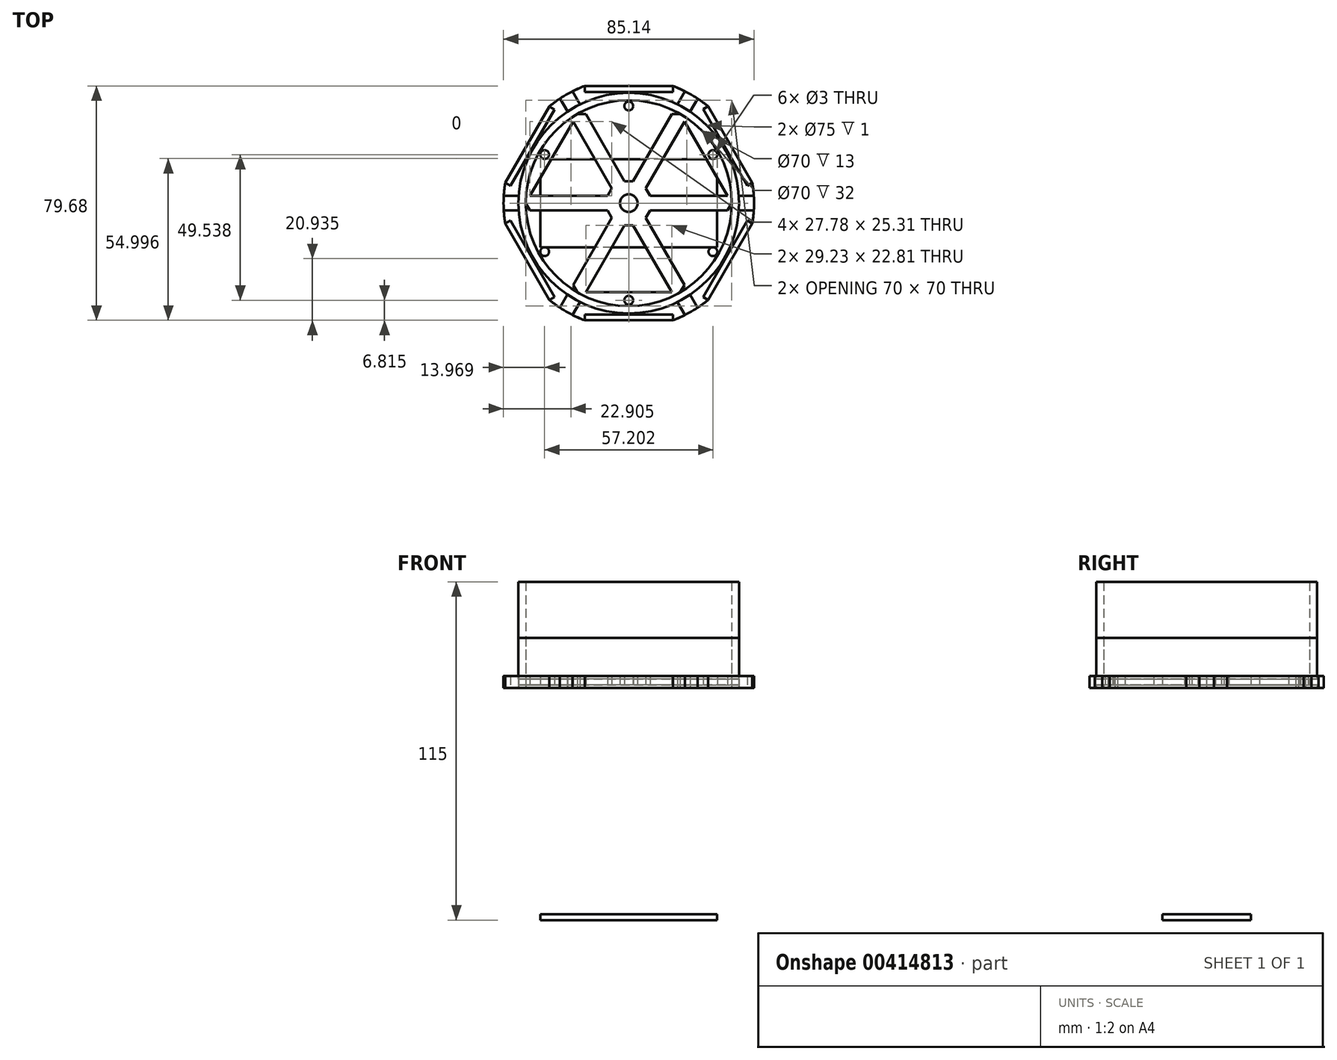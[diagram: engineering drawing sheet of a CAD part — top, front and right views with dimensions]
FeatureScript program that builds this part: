
annotation { "Feature Type Name" : "Feature", "Feature Type Description" : "" }
export const myFeature = defineFeature(function(context is Context, id is Id, definition is map)
    precondition{}
    {
        {
            var Q0;
            Q0=qCreatedBy(makeId("Front.planeOp"),FACE);
            var sketch = newSketch(context, id + "F0", { "sketchPlane" : qUnion([Q0])});
            skPoint(sketch, "E0.0.midPoint", {"position": v(34.2, -19.75) * mm});
            skLineSegment(sketch, "E1", {"start": v(-48.36, -0.03) * mm, "end": v(42.86, 0) * mm, "construction": true});
            skLineSegment(sketch, "E2", {"start": v(21.2, 36.7) * mm, "end": v(-22.8, -39.5) * mm, "construction": true});
            skLineSegment(sketch, "E3", {"start": v(-21.15, 36.67) * mm, "end": v(22.83, -39.49) * mm, "construction": true});
            skLineSegment(sketch, "E4.bottom", {"start": v(15.02, 37.52) * mm, "end": v(-14.98, 37.51) * mm});
            skLineSegment(sketch, "E4.left", {"start": v(15.02, 37.52) * mm, "end": v(15.07, 39.6) * mm});
            skLineSegment(sketch, "E4.right", {"start": v(-14.98, 37.51) * mm, "end": v(-14.93, 39.62) * mm});
            skPoint(sketch, "E4.middle", {"position": v(-0.03, 39.48) * mm});
            skCircle(sketch, "E5", {"center": v(0, 0) * mm, "radius": 37.5 * mm});
            skLineSegment(sketch, "E6", {"start": v(19, 37.88) * mm, "end": v(16.67, 33.87) * mm});
            skLineSegment(sketch, "E7", {"start": v(16.67, 33.87) * mm, "end": v(18.84, 32.62) * mm});
            skLineSegment(sketch, "E8.MirrorCS", {"start": v(21, 31.37) * mm, "end": v(18.84, 32.62) * mm});
            skLineSegment(sketch, "E9.MirrorCS", {"start": v(23.32, 35.38) * mm, "end": v(21, 31.37) * mm});
            skLineSegment(sketch, "E10.MirrorCS", {"start": v(25, 31.76) * mm, "end": v(26.77, 32.85) * mm});
            skLineSegment(sketch, "E11.MirrorCS", {"start": v(25, 31.76) * mm, "end": v(40, 5.78) * mm});
            skLineSegment(sketch, "E12.MirrorCS", {"start": v(40, 5.78) * mm, "end": v(41.68, 6.81) * mm});
            skLineSegment(sketch, "E13.MirrorCS", {"start": v(-18.97, 37.85) * mm, "end": v(-16.67, 33.87) * mm});
            skLineSegment(sketch, "E14.MirrorCS", {"start": v(-23.3, 35.35) * mm, "end": v(-21, 31.37) * mm});
            skLineSegment(sketch, "E15.MirrorCS", {"start": v(-21, 31.37) * mm, "end": v(-18.84, 32.62) * mm});
            skLineSegment(sketch, "E16.MirrorCS", {"start": v(-16.67, 33.87) * mm, "end": v(-18.84, 32.62) * mm});
            skArc(sketch, "E17", {"start": v(-14.93, 39.62) * mm, "mid": v(-16.97, 38.78) * mm, "end": v(-18.97, 37.85) * mm});
            skArc(sketch, "E18", {"start": v(15.07, 39.6) * mm, "mid": v(17.05, 38.8) * mm, "end": v(19, 37.88) * mm});
            skLineSegment(sketch, "E19.MirrorCS", {"start": v(-39.96, 5.77) * mm, "end": v(-24.96, 31.75) * mm});
            skLineSegment(sketch, "E20.MirrorCS", {"start": v(-24.96, 31.75) * mm, "end": v(-26.81, 32.75) * mm});
            skLineSegment(sketch, "E21.MirrorCS", {"start": v(-39.96, 5.77) * mm, "end": v(-41.8, 6.77) * mm});
            skArc(sketch, "E22.trimOffspring", {"start": v(-23.3, 35.35) * mm, "mid": v(-25.04, 34.13) * mm, "end": v(-26.72, 32.84) * mm});
            skArc(sketch, "E23.trimOffspring", {"start": v(23.32, 35.38) * mm, "mid": v(25.08, 34.16) * mm, "end": v(26.77, 32.85) * mm});
            skLineSegment(sketch, "E24", {"start": v(0, 0) * mm, "end": v(32.5, 18.77) * mm, "construction": true});
            skLineSegment(sketch, "E25", {"start": v(0, 0) * mm, "end": v(-32.46, 18.76) * mm, "construction": true});
            skArc(sketch, "E26.MirrorCS", {"start": v(42.3, 2.52) * mm, "mid": v(42.12, 4.65) * mm, "end": v(41.83, 6.77) * mm});
            skLineSegment(sketch, "E27.MirrorCS", {"start": v(42.3, 2.52) * mm, "end": v(37.67, 2.52) * mm});
            skLineSegment(sketch, "E28.MirrorCS", {"start": v(37.67, 2.52) * mm, "end": v(37.67, 0.02) * mm});
            skArc(sketch, "E29.MirrorCS", {"start": v(-42.26, 2.55) * mm, "mid": v(-42.08, 4.66) * mm, "end": v(-41.8, 6.76) * mm});
            skLineSegment(sketch, "E30.MirrorCS", {"start": v(-42.26, 2.55) * mm, "end": v(-37.67, 2.54) * mm});
            skLineSegment(sketch, "E31.MirrorCS", {"start": v(-37.67, 2.54) * mm, "end": v(-37.67, 0.04) * mm});
            skLineSegment(sketch, "E32.MirrorCS", {"start": v(25.02, -31.76) * mm, "end": v(26.8, -32.85) * mm});
            skLineSegment(sketch, "E33.MirrorCS", {"start": v(-39.95, -5.83) * mm, "end": v(-41.8, -6.82) * mm});
            skLineSegment(sketch, "E34.MirrorCS", {"start": v(40, -5.77) * mm, "end": v(41.68, -6.8) * mm});
            skLineSegment(sketch, "E35.MirrorCS", {"start": v(-24.93, -31.8) * mm, "end": v(-26.78, -32.8) * mm});
            skArc(sketch, "E36.MirrorCS", {"start": v(23.35, -35.39) * mm, "mid": v(25.1, -34.16) * mm, "end": v(26.8, -32.85) * mm});
            skLineSegment(sketch, "E37.MirrorCS", {"start": v(16.7, -33.88) * mm, "end": v(18.87, -32.63) * mm});
            skLineSegment(sketch, "E38.MirrorCS", {"start": v(21.03, -31.37) * mm, "end": v(18.87, -32.63) * mm});
            skLineSegment(sketch, "E39.MirrorCS", {"start": v(-20.98, -31.41) * mm, "end": v(-18.81, -32.66) * mm});
            skLineSegment(sketch, "E40.MirrorCS", {"start": v(-16.65, -33.9) * mm, "end": v(-18.81, -32.66) * mm});
            skArc(sketch, "E41.MirrorCS", {"start": v(-23.27, -35.39) * mm, "mid": v(-25.01, -34.18) * mm, "end": v(-26.7, -32.88) * mm});
            skLineSegment(sketch, "E42.MirrorCS", {"start": v(-23.27, -35.39) * mm, "end": v(-20.98, -31.41) * mm});
            skLineSegment(sketch, "E43.MirrorCS", {"start": v(25.02, -31.76) * mm, "end": v(40, -5.77) * mm});
            skLineSegment(sketch, "E44.MirrorCS", {"start": v(-39.95, -5.83) * mm, "end": v(-24.93, -31.8) * mm});
            skPoint(sketch, "E45.MirrorP", {"position": v(0, -39.5) * mm});
            skLineSegment(sketch, "E46.MirrorCS", {"start": v(42.3, -2.5) * mm, "end": v(37.67, -2.51) * mm});
            skArc(sketch, "E47.MirrorCS", {"start": v(-42.26, -2.6) * mm, "mid": v(-42.07, -4.72) * mm, "end": v(-41.79, -6.82) * mm});
            skArc(sketch, "E48.MirrorCS", {"start": v(42.3, -2.5) * mm, "mid": v(42.13, -4.64) * mm, "end": v(41.84, -6.76) * mm});
            skLineSegment(sketch, "E49.MirrorCS", {"start": v(23.35, -35.39) * mm, "end": v(21.03, -31.37) * mm});
            skLineSegment(sketch, "E50.MirrorCS", {"start": v(15.05, -37.53) * mm, "end": v(-14.95, -37.55) * mm});
            skLineSegment(sketch, "E51.MirrorCS", {"start": v(15.05, -37.53) * mm, "end": v(15.1, -39.62) * mm});
            skArc(sketch, "E52.MirrorCS", {"start": v(15.1, -39.62) * mm, "mid": v(17.09, -38.8) * mm, "end": v(19.02, -37.9) * mm});
            skLineSegment(sketch, "E53.MirrorCS", {"start": v(19.02, -37.9) * mm, "end": v(16.7, -33.88) * mm});
            skLineSegment(sketch, "E54.MirrorCS", {"start": v(-14.95, -37.55) * mm, "end": v(-14.9, -39.65) * mm});
            skArc(sketch, "E55.MirrorCS", {"start": v(-14.9, -39.65) * mm, "mid": v(-16.94, -38.82) * mm, "end": v(-18.94, -37.89) * mm});
            skLineSegment(sketch, "E56.MirrorCS", {"start": v(-18.94, -37.89) * mm, "end": v(-16.65, -33.9) * mm});
            skCircle(sketch, "E57.cCircle", {"center": v(0, 0) * mm, "radius": 35.5 * mm});
            skLineSegment(sketch, "E57.0", {"start": v(35.5, 0) * mm, "end": v(17.75, -30.74) * mm});
            skLineSegment(sketch, "E57.1", {"start": v(17.75, -30.74) * mm, "end": v(-17.75, -30.75) * mm});
            skLineSegment(sketch, "E57.2", {"start": v(-17.75, -30.75) * mm, "end": v(-35.5, 0) * mm});
            skLineSegment(sketch, "E57.3", {"start": v(-35.5, 0) * mm, "end": v(-17.75, 30.74) * mm});
            skLineSegment(sketch, "E57.4", {"start": v(-17.75, 30.74) * mm, "end": v(17.75, 30.75) * mm});
            skLineSegment(sketch, "E57.5", {"start": v(17.75, 30.75) * mm, "end": v(35.5, 0) * mm});
            skLineSegment(sketch, "E58.0", {"start": v(7.6, 0) * mm, "end": v(3.75, -6.55) * mm});
            skLineSegment(sketch, "E58.1", {"start": v(3.75, -6.55) * mm, "end": v(-3.81, -6.54) * mm});
            skLineSegment(sketch, "E58.2", {"start": v(-3.81, -6.54) * mm, "end": v(-7.65, 0) * mm});
            skLineSegment(sketch, "E58.3", {"start": v(-7.65, 0) * mm, "end": v(-3.79, 6.55) * mm});
            skLineSegment(sketch, "E58.4", {"start": v(-3.79, 6.55) * mm, "end": v(3.76, 6.54) * mm});
            skLineSegment(sketch, "E58.5", {"start": v(3.76, 6.54) * mm, "end": v(7.6, 0) * mm});
            skLineSegment(sketch, "E59", {"start": v(21, 31.37) * mm, "end": v(5.23, 4.04) * mm, "construction": true});
            skLineSegment(sketch, "E60", {"start": v(19.2, 28.24) * mm, "end": v(5.23, 4.04) * mm});
            skLineSegment(sketch, "E61.MirrorCS", {"start": v(16.67, 33.87) * mm, "end": v(0.9, 6.54) * mm, "construction": true});
            skLineSegment(sketch, "E62", {"start": v(14.87, 30.75) * mm, "end": v(0.9, 6.54) * mm});
            skLineSegment(sketch, "E63.MirrorCS", {"start": v(-16.67, 33.87) * mm, "end": v(-0.9, 6.54) * mm, "construction": true});
            skLineSegment(sketch, "E64.MirrorCS", {"start": v(-21, 31.37) * mm, "end": v(-5.23, 4.04) * mm, "construction": true});
            skLineSegment(sketch, "E65", {"start": v(-14.87, 30.74) * mm, "end": v(-0.9, 6.54) * mm});
            skLineSegment(sketch, "E66", {"start": v(-19.2, 28.24) * mm, "end": v(-5.23, 4.04) * mm});
            skLineSegment(sketch, "E67.MirrorCS", {"start": v(37.67, 2.52) * mm, "end": v(6.11, 2.51) * mm, "construction": true});
            skLineSegment(sketch, "E68.MirrorCS", {"start": v(37.67, -2.48) * mm, "end": v(6.11, -2.49) * mm, "construction": true});
            skLineSegment(sketch, "E69.MirrorCS", {"start": v(21, -31.37) * mm, "end": v(5.22, -4.05) * mm, "construction": true});
            skLineSegment(sketch, "E70.MirrorCS", {"start": v(16.68, -33.87) * mm, "end": v(0.89, -6.55) * mm, "construction": true});
            skLineSegment(sketch, "E71", {"start": v(34.05, 2.52) * mm, "end": v(6.11, 2.51) * mm});
            skLineSegment(sketch, "E72", {"start": v(34.07, -2.48) * mm, "end": v(6.11, -2.49) * mm});
            skLineSegment(sketch, "E73", {"start": v(5.22, -4.05) * mm, "end": v(19.2, -28.24) * mm});
            skLineSegment(sketch, "E74", {"start": v(0.89, -6.55) * mm, "end": v(14.87, -30.74) * mm});
            skLineSegment(sketch, "E75.MirrorCS", {"start": v(-16.68, -33.87) * mm, "end": v(-0.89, -6.55) * mm, "construction": true});
            skLineSegment(sketch, "E76.MirrorCS", {"start": v(-21, -31.37) * mm, "end": v(-5.25, -4.1) * mm, "construction": true});
            skLineSegment(sketch, "E77.MirrorCS", {"start": v(-37.67, -2.48) * mm, "end": v(-6.11, -2.49) * mm, "construction": true});
            skLineSegment(sketch, "E78.MirrorCS", {"start": v(-37.67, 2.52) * mm, "end": v(-6.11, 2.51) * mm, "construction": true});
            skLineSegment(sketch, "E79", {"start": v(-14.87, -30.75) * mm, "end": v(-0.89, -6.55) * mm});
            skLineSegment(sketch, "E80", {"start": v(-19.2, -28.24) * mm, "end": v(-5.25, -4.1) * mm});
            skLineSegment(sketch, "E81", {"start": v(-6.11, -2.49) * mm, "end": v(-34.07, -2.48) * mm});
            skLineSegment(sketch, "E82", {"start": v(-34.04, 2.52) * mm, "end": v(-6.11, 2.51) * mm});
            skCircle(sketch, "E83", {"center": v(0, 33.97) * mm, "radius": 1.5 * mm});
            skCircle(sketch, "E84.MirrorC", {"center": v(29.43, 16.98) * mm, "radius": 1.5 * mm});
            skCircle(sketch, "E85.MirrorC", {"center": v(-29.38, 17) * mm, "radius": 1.5 * mm});
            skCircle(sketch, "E86.MirrorC", {"center": v(0.03, -34) * mm, "radius": 1.5 * mm});
            skCircle(sketch, "E87.MirrorC", {"center": v(29.44, -16.98) * mm, "radius": 1.5 * mm});
            skCircle(sketch, "E88.MirrorC", {"center": v(-29.37, -17.05) * mm, "radius": 1.5 * mm});
            skLineSegment(sketch, "E89.MirrorCS", {"start": v(-37.67, -2.46) * mm, "end": v(-37.67, 0.04) * mm});
            skLineSegment(sketch, "E90.MirrorCS", {"start": v(-42.26, -2.45) * mm, "end": v(-37.67, -2.46) * mm});
            skLineSegment(sketch, "E91.MirrorCS", {"start": v(37.67, -2.48) * mm, "end": v(37.67, 0.02) * mm});
            skPoint(sketch, "E92.orphan", {"position": v(-5.22, -4.05) * mm});
            skSolve(sketch);
        }
        {
            var Q0;
            Q0=qCreatedBy(makeId("Top.planeOp"),FACE);
            var sketch = newSketch(context, id + "F1", { "sketchPlane" : qUnion([Q0])});
            skCircle(sketch, "E93.cCircle", {"center": v(0, 0) * mm, "radius": 46 * mm, "construction": true});
            skLineSegment(sketch, "E94", {"start": v(-23, 39.84) * mm, "end": v(23, -39.84) * mm, "construction": true});
            skLineSegment(sketch, "E95", {"start": v(-23, -39.84) * mm, "end": v(23, 39.84) * mm, "construction": true});
            skLineSegment(sketch, "E96", {"start": v(-46, 0) * mm, "end": v(46, 0) * mm, "construction": true});
            skCircle(sketch, "E97", {"center": v(0, 0) * mm, "radius": 37.5 * mm});
            skLineSegment(sketch, "E98.bottom", {"start": v(15, -37.84) * mm, "end": v(-15, -37.84) * mm});
            skLineSegment(sketch, "E98.left", {"start": v(15, -37.84) * mm, "end": v(15, -39.84) * mm});
            skLineSegment(sketch, "E98.right", {"start": v(-15, -37.84) * mm, "end": v(-15, -39.84) * mm});
            skPoint(sketch, "E98.middle", {"position": v(0, -39.84) * mm});
            skLineSegment(sketch, "E99", {"start": v(0, 0) * mm, "end": v(32.77, -18.92) * mm, "construction": true});
            skLineSegment(sketch, "E100", {"start": v(0, 0) * mm, "end": v(-32.77, 18.92) * mm, "construction": true});
            skLineSegment(sketch, "E101", {"start": v(0, 0) * mm, "end": v(32.77, 18.92) * mm, "construction": true});
            skLineSegment(sketch, "E102.top", {"start": v(15, 37.84) * mm, "end": v(-15, 37.84) * mm});
            skLineSegment(sketch, "E102.left", {"start": v(15, 39.84) * mm, "end": v(15, 37.84) * mm});
            skLineSegment(sketch, "E102.right", {"start": v(-15, 39.84) * mm, "end": v(-15, 37.84) * mm});
            skPoint(sketch, "E102.middle", {"position": v(0, 39.84) * mm});
            skLineSegment(sketch, "E103", {"start": v(-32.77, -18.92) * mm, "end": v(-40.27, -5.93) * mm});
            skLineSegment(sketch, "E104", {"start": v(-40.27, -5.93) * mm, "end": v(-42, -6.93) * mm});
            skLineSegment(sketch, "E105", {"start": v(-32.77, -18.92) * mm, "end": v(-25.27, -31.9) * mm});
            skLineSegment(sketch, "E106", {"start": v(-25.27, -31.9) * mm, "end": v(-27, -32.9) * mm});
            skLineSegment(sketch, "E107", {"start": v(32.77, -18.92) * mm, "end": v(40.27, -5.93) * mm});
            skLineSegment(sketch, "E108", {"start": v(40.27, -5.93) * mm, "end": v(42, -6.93) * mm});
            skLineSegment(sketch, "E109", {"start": v(32.77, -18.92) * mm, "end": v(25.27, -31.9) * mm});
            skLineSegment(sketch, "E110", {"start": v(25.27, -31.9) * mm, "end": v(27, -32.9) * mm});
            skLineSegment(sketch, "E111", {"start": v(32.77, 18.92) * mm, "end": v(25.27, 31.9) * mm});
            skLineSegment(sketch, "E112", {"start": v(25.27, 31.9) * mm, "end": v(27, 32.9) * mm});
            skLineSegment(sketch, "E113", {"start": v(32.77, 18.92) * mm, "end": v(40.27, 5.93) * mm});
            skLineSegment(sketch, "E114", {"start": v(40.27, 5.93) * mm, "end": v(42, 6.93) * mm});
            skLineSegment(sketch, "E115", {"start": v(-32.78, 18.9) * mm, "end": v(-25.28, 31.89) * mm});
            skLineSegment(sketch, "E116", {"start": v(-25.28, 31.89) * mm, "end": v(-27.01, 32.89) * mm});
            skLineSegment(sketch, "E117", {"start": v(-32.78, 18.9) * mm, "end": v(-40.28, 5.9) * mm});
            skLineSegment(sketch, "E118", {"start": v(-40.28, 5.9) * mm, "end": v(-42.01, 6.9) * mm});
            skPoint(sketch, "E119.orphan", {"position": v(-15, 41.84) * mm});
            skPoint(sketch, "E120.orphan", {"position": v(15, 41.84) * mm});
            skPoint(sketch, "E121.start.orphan", {"position": v(34.52, 19.93) * mm});
            skLineSegment(sketch, "E122.trimOffspring", {"start": v(-27.01, 32.89) * mm, "end": v(-27, 32.9) * mm});
            skPoint(sketch, "E123.start.orphan", {"position": v(-34.5, 19.92) * mm});
            skPoint(sketch, "E124.orphan", {"position": v(15, -41.84) * mm});
            skPoint(sketch, "E125.orphan", {"position": v(-15, -41.84) * mm});
            skCircle(sketch, "E126", {"center": v(0, 0) * mm, "radius": 35 * mm, "construction": true});
            skCircle(sketch, "E127.cCircle", {"center": v(0, 0) * mm, "radius": 35 * mm});
            skLineSegment(sketch, "E127.0", {"start": v(-17.5, -30.31) * mm, "end": v(-35, 0) * mm});
            skLineSegment(sketch, "E127.1", {"start": v(-35, 0) * mm, "end": v(-17.5, 30.31) * mm});
            skLineSegment(sketch, "E127.2", {"start": v(-17.5, 30.31) * mm, "end": v(17.5, 30.31) * mm});
            skLineSegment(sketch, "E127.3", {"start": v(17.5, 30.31) * mm, "end": v(35, 0) * mm});
            skLineSegment(sketch, "E127.4", {"start": v(35, 0) * mm, "end": v(17.5, -30.31) * mm});
            skLineSegment(sketch, "E127.5", {"start": v(17.5, -30.31) * mm, "end": v(-17.5, -30.31) * mm});
            skArc(sketch, "E128", {"start": v(27, 32.9) * mm, "mid": v(25.22, 34.29) * mm, "end": v(23.38, 35.57) * mm});
            skArc(sketch, "E129", {"start": v(-15, 39.84) * mm, "mid": v(-17.08, 38.99) * mm, "end": v(-19.12, 38.03) * mm});
            skArc(sketch, "E130", {"start": v(42, -6.93) * mm, "mid": v(42.3, -4.72) * mm, "end": v(42.5, -2.5) * mm});
            skArc(sketch, "E131", {"start": v(-42, -6.93) * mm, "mid": v(-42.3, -4.72) * mm, "end": v(-42.5, -2.5) * mm});
            skArc(sketch, "E132", {"start": v(-27, -32.9) * mm, "mid": v(-25.24, -34.28) * mm, "end": v(-23.41, -35.55) * mm});
            skArc(sketch, "E133", {"start": v(15, -39.84) * mm, "mid": v(17.06, -39) * mm, "end": v(19.08, -38.05) * mm});
            skPoint(sketch, "E93.5.start.orphan", {"position": v(23.04, 39.86) * mm});
            skPoint(sketch, "E93.1.start.orphan", {"position": v(23, -39.84) * mm});
            skArc(sketch, "E134", {"start": v(23.41, -35.55) * mm, "mid": v(36.86, -21.28) * mm, "end": v(42.5, -2.5) * mm, "construction": true});
            skLineSegment(sketch, "E135", {"start": v(-16.58, 33.64) * mm, "end": v(-19.12, 38.03) * mm});
            skLineSegment(sketch, "E136.MirrorCS", {"start": v(-20.84, 31.18) * mm, "end": v(-23.38, 35.57) * mm});
            skLineSegment(sketch, "E137.MirrorCS", {"start": v(16.58, 33.64) * mm, "end": v(19.12, 38.03) * mm});
            skLineSegment(sketch, "E138.MirrorCS", {"start": v(20.84, 31.18) * mm, "end": v(23.38, 35.57) * mm});
            skLineSegment(sketch, "E139", {"start": v(42.5, 2.5) * mm, "end": v(37.42, 2.5) * mm});
            skLineSegment(sketch, "E140.MirrorCS", {"start": v(42.5, -2.5) * mm, "end": v(37.42, -2.5) * mm});
            skArc(sketch, "E141", {"start": v(37.42, -2.5) * mm, "mid": v(37.5, 0) * mm, "end": v(37.42, 2.5) * mm});
            skArc(sketch, "E142", {"start": v(20.84, 31.18) * mm, "mid": v(18.75, 32.48) * mm, "end": v(16.58, 33.64) * mm});
            skArc(sketch, "E143", {"start": v(-16.58, 33.64) * mm, "mid": v(-18.75, 32.48) * mm, "end": v(-20.84, 31.18) * mm});
            skLineSegment(sketch, "E144.MirrorCS", {"start": v(-42.5, 2.5) * mm, "end": v(-37.42, 2.5) * mm});
            skLineSegment(sketch, "E145.MirrorCS", {"start": v(-42.5, -2.5) * mm, "end": v(-37.42, -2.5) * mm});
            skArc(sketch, "E146", {"start": v(-37.42, 2.5) * mm, "mid": v(-37.5, 0) * mm, "end": v(-37.42, -2.5) * mm});
            skLineSegment(sketch, "E147", {"start": v(-19.08, -38.05) * mm, "end": v(-16.54, -33.65) * mm});
            skLineSegment(sketch, "E148.MirrorCS", {"start": v(-23.41, -35.55) * mm, "end": v(-20.87, -31.15) * mm});
            skArc(sketch, "E149", {"start": v(-16.54, -33.65) * mm, "mid": v(-18.75, -32.48) * mm, "end": v(-20.87, -31.15) * mm});
            skLineSegment(sketch, "E150", {"start": v(23.41, -35.55) * mm, "end": v(20.87, -31.15) * mm});
            skLineSegment(sketch, "E151.MirrorCS", {"start": v(19.08, -38.05) * mm, "end": v(16.54, -33.65) * mm});
            skArc(sketch, "E152", {"start": v(16.54, -33.65) * mm, "mid": v(18.75, -32.48) * mm, "end": v(20.87, -31.15) * mm});
            skArc(sketch, "E153.trimOffspring", {"start": v(23.41, -35.55) * mm, "mid": v(25.24, -34.28) * mm, "end": v(27, -32.9) * mm});
            skArc(sketch, "E154.trimOffspring", {"start": v(-19.08, -38.05) * mm, "mid": v(0, -42.57) * mm, "end": v(19.08, -38.05) * mm, "construction": true});
            skArc(sketch, "E155.trimOffspring", {"start": v(-19.08, -38.05) * mm, "mid": v(-17.06, -39) * mm, "end": v(-15, -39.84) * mm});
            skArc(sketch, "E156.trimOffspring", {"start": v(19.12, 38.03) * mm, "mid": v(0, 42.57) * mm, "end": v(-19.12, 38.03) * mm, "construction": true});
            skArc(sketch, "E157.trimOffspring", {"start": v(19.12, 38.03) * mm, "mid": v(17.08, 38.99) * mm, "end": v(15, 39.84) * mm});
            skArc(sketch, "E158.trimOffspring", {"start": v(-23.38, 35.57) * mm, "mid": v(-36.85, 21.3) * mm, "end": v(-42.5, 2.5) * mm, "construction": true});
            skArc(sketch, "E159.trimOffspring", {"start": v(-23.38, 35.57) * mm, "mid": v(-25.22, 34.29) * mm, "end": v(-27, 32.9) * mm});
            skArc(sketch, "E160.trimOffspring", {"start": v(-42.5, -2.5) * mm, "mid": v(-37.93, -19.33) * mm, "end": v(-27, -32.9) * mm, "construction": true});
            skArc(sketch, "E161.trimOffspring", {"start": v(-42.5, 2.5) * mm, "mid": v(-42.3, 4.7) * mm, "end": v(-42, 6.9) * mm});
            skArc(sketch, "E162.trimOffspring", {"start": v(42.5, 2.5) * mm, "mid": v(36.85, 21.3) * mm, "end": v(23.38, 35.57) * mm, "construction": true});
            skArc(sketch, "E163.trimOffspring", {"start": v(42.5, 2.5) * mm, "mid": v(42.3, 4.72) * mm, "end": v(42, 6.93) * mm});
            skCircle(sketch, "E164.cCircle", {"center": v(0, 0) * mm, "radius": 8.66 * mm, "construction": true});
            skLineSegment(sketch, "E164.0", {"start": v(-4.33, 7.5) * mm, "end": v(4.33, 7.5) * mm});
            skLineSegment(sketch, "E164.1", {"start": v(4.33, 7.5) * mm, "end": v(8.66, 0) * mm});
            skLineSegment(sketch, "E164.2", {"start": v(8.66, 0) * mm, "end": v(4.33, -7.5) * mm});
            skLineSegment(sketch, "E164.3", {"start": v(4.33, -7.5) * mm, "end": v(-4.33, -7.5) * mm});
            skLineSegment(sketch, "E164.4", {"start": v(-4.33, -7.5) * mm, "end": v(-8.66, 0) * mm});
            skLineSegment(sketch, "E164.5", {"start": v(-8.66, 0) * mm, "end": v(-4.33, 7.5) * mm});
            skLineSegment(sketch, "E165", {"start": v(-7.22, 2.5) * mm, "end": v(-33.56, 2.5) * mm});
            skLineSegment(sketch, "E166.MirrorCS", {"start": v(-7.22, -2.5) * mm, "end": v(-33.56, -2.5) * mm});
            skLineSegment(sketch, "E167.MirrorCS", {"start": v(7.22, 2.5) * mm, "end": v(33.56, 2.5) * mm});
            skLineSegment(sketch, "E168.MirrorCS", {"start": v(7.22, -2.5) * mm, "end": v(33.56, -2.5) * mm});
            skLineSegment(sketch, "E169.MirrorCS", {"start": v(-5.77, 5) * mm, "end": v(-18.94, 27.81) * mm});
            skLineSegment(sketch, "E170.MirrorCS", {"start": v(-1.44, 7.5) * mm, "end": v(-14.61, 30.31) * mm});
            skLineSegment(sketch, "E171.MirrorCS", {"start": v(1.44, 7.5) * mm, "end": v(14.61, 30.31) * mm});
            skLineSegment(sketch, "E172.MirrorCS", {"start": v(5.77, 5) * mm, "end": v(18.94, 27.81) * mm});
            skLineSegment(sketch, "E173.MirrorCS", {"start": v(5.77, -5) * mm, "end": v(18.94, -27.81) * mm});
            skLineSegment(sketch, "E174.MirrorCS", {"start": v(1.44, -7.5) * mm, "end": v(14.61, -30.31) * mm});
            skLineSegment(sketch, "E175.MirrorCS", {"start": v(-1.44, -7.5) * mm, "end": v(-14.61, -30.31) * mm});
            skLineSegment(sketch, "E176.MirrorCS", {"start": v(-5.77, -5) * mm, "end": v(-18.94, -27.81) * mm});
            skCircle(sketch, "E177", {"center": v(0, 0) * mm, "radius": 3 * mm});
            skCircle(sketch, "E178", {"center": v(28.6, 16.51) * mm, "radius": 1.5 * mm});
            skCircle(sketch, "E179.MirrorC", {"center": v(0, 33.03) * mm, "radius": 1.5 * mm});
            skCircle(sketch, "E180.MirrorC", {"center": v(-28.6, 16.51) * mm, "radius": 1.5 * mm});
            skCircle(sketch, "E181.MirrorC", {"center": v(28.6, -16.51) * mm, "radius": 1.5 * mm});
            skCircle(sketch, "E182.MirrorC", {"center": v(0, -33.03) * mm, "radius": 1.5 * mm});
            skCircle(sketch, "E183.MirrorC", {"center": v(-28.6, -16.51) * mm, "radius": 1.5 * mm});
            skLineSegment(sketch, "E184", {"start": v(15, -39.84) * mm, "end": v(-15, -39.84) * mm});
            skLineSegment(sketch, "E185", {"start": v(-27, -32.9) * mm, "end": v(-42, -6.93) * mm});
            skLineSegment(sketch, "E186", {"start": v(27, -32.9) * mm, "end": v(42, -6.93) * mm});
            skLineSegment(sketch, "E187", {"start": v(42, 6.93) * mm, "end": v(27, 32.9) * mm});
            skLineSegment(sketch, "E188", {"start": v(-27, 32.9) * mm, "end": v(-42, 6.9) * mm});
            skLineSegment(sketch, "E189", {"start": v(15, 39.84) * mm, "end": v(-15, 39.84) * mm});
            skCircle(sketch, "E190", {"center": v(0, 0) * mm, "radius": 42.57 * mm});
            skSolve(sketch);
        }
        {
            var Q0;
            Q0=makeQuery(id+"F1.imprint","IMPRINT",FACE,{"disambiguationData":[TD([[makeQuery(id+"F1.imprint","IMPRINT",EDGE,{"derivedFrom":sQuery(id+"F1.wireOp",EDGE,"E98.bottom")}),-1.0]])]});
            var Q1;
            {var subQ3=sQuery(id+"F1.wireOp",EDGE,"E175.MirrorCS");Q1=makeQuery(id+"F1.imprint","IMPRINT",FACE,{"disambiguationData":[TD([[makeQuery(id+"F1.imprint","IMPRINT",EDGE,{"derivedFrom":subQ3}),-1.0]])]});}
            var Q2;
            {var subQ4=sQuery(id+"F1.wireOp",EDGE,"E169.MirrorCS");Q2=makeQuery(id+"F1.imprint","IMPRINT",FACE,{"disambiguationData":[TD([[makeQuery(id+"F1.imprint","IMPRINT",EDGE,{"derivedFrom":subQ4}),-1.0]])]});}
            var Q3;
            {var subQ3=sQuery(id+"F1.wireOp",EDGE,"E165");Q3=makeQuery(id+"F1.imprint","IMPRINT",FACE,{"disambiguationData":[TD([[makeQuery(id+"F1.imprint","IMPRINT",EDGE,{"derivedFrom":subQ3}),1.0]])]});}
            var Q4;
            {var subQ4=sQuery(id+"F1.wireOp",EDGE,"E171.MirrorCS");Q4=makeQuery(id+"F1.imprint","IMPRINT",FACE,{"disambiguationData":[TD([[makeQuery(id+"F1.imprint","IMPRINT",EDGE,{"derivedFrom":subQ4}),-1.0]])]});}
            var Q5;
            {var subQ4=sQuery(id+"F1.wireOp",EDGE,"E167.MirrorCS");Q5=makeQuery(id+"F1.imprint","IMPRINT",FACE,{"disambiguationData":[TD([[makeQuery(id+"F1.imprint","IMPRINT",EDGE,{"derivedFrom":subQ4}),-1.0]])]});}
            var Q6;
            {var subQ4=sQuery(id+"F1.wireOp",EDGE,"E173.MirrorCS");Q6=makeQuery(id+"F1.imprint","IMPRINT",FACE,{"disambiguationData":[TD([[makeQuery(id+"F1.imprint","IMPRINT",EDGE,{"derivedFrom":subQ4}),-1.0]])]});}
            var Q7;
            {var subQ10=sQuery(id+"F1.wireOp",EDGE,"E164.5");var subQ11=sQuery(id+"F1.wireOp",EDGE,"E164.0");var subQ12=makeQuery(id+"F1.imprint","INTERSECT",VERTEX,{"derivedFrom":[subQ11,subQ10]});Q7=makeQuery(id+"F1.imprint","IMPRINT",FACE,{"disambiguationData":[TD([[makeQuery(id+"F1.imprint","IMPRINT",EDGE,{"disambiguationData":[TD([[subQ12,-1.0]])],"derivedFrom":subQ11}),-1.0]])]});}
            var Q8;
            Q8=makeQuery(id+"F1.imprint","IMPRINT",FACE,{"disambiguationData":[TD([[makeQuery(id+"F1.imprint","IMPRINT",EDGE,{"derivedFrom":sQuery(id+"F1.wireOp",EDGE,"E178")}),-1.0]])]});
            var Q9;
            {var subQ0=sQuery(id+"F1.wireOp",EDGE,"E97");var subQ8=makeQuery(id+"F1.imprint","INTERSECT",VERTEX,{"derivedFrom":[subQ0,sQuery(id+"F1.wireOp",EDGE,"E138.MirrorCS")]});Q9=makeQuery(id+"F1.imprint","IMPRINT",FACE,{"disambiguationData":[TD([[makeQuery(id+"F1.imprint","IMPRINT",EDGE,{"disambiguationData":[TD([[subQ8,1.0]])],"derivedFrom":subQ0}),1.0]])]});}
            var Q10;
            Q10=makeQuery(id+"F1.imprint","IMPRINT",FACE,{"disambiguationData":[TD([[makeQuery(id+"F1.imprint","IMPRINT",EDGE,{"derivedFrom":sQuery(id+"F1.wireOp",EDGE,"E111")}),1.0]])]});
            var Q11;
            Q11=makeQuery(id+"F1.imprint","IMPRINT",FACE,{"disambiguationData":[TD([[makeQuery(id+"F1.imprint","IMPRINT",EDGE,{"derivedFrom":sQuery(id+"F1.wireOp",EDGE,"E102.top")}),1.0]])]});
            var Q12;
            Q12=makeQuery(id+"F1.imprint","IMPRINT",FACE,{"disambiguationData":[TD([[makeQuery(id+"F1.imprint","IMPRINT",EDGE,{"derivedFrom":sQuery(id+"F1.wireOp",EDGE,"E115")}),-1.0]])]});
            var Q13;
            Q13=makeQuery(id+"F1.imprint","IMPRINT",FACE,{"disambiguationData":[TD([[makeQuery(id+"F1.imprint","IMPRINT",EDGE,{"derivedFrom":sQuery(id+"F1.wireOp",EDGE,"E103")}),-1.0]])]});
            var Q14;
            Q14=makeQuery(id+"F1.imprint","IMPRINT",FACE,{"disambiguationData":[TD([[makeQuery(id+"F1.imprint","IMPRINT",EDGE,{"derivedFrom":sQuery(id+"F1.wireOp",EDGE,"E183.MirrorC")}),1.0]])]});
            var Q15;
            Q15=makeQuery(id+"F1.imprint","IMPRINT",FACE,{"disambiguationData":[TD([[makeQuery(id+"F1.imprint","IMPRINT",EDGE,{"derivedFrom":sQuery(id+"F1.wireOp",EDGE,"E107")}),1.0]])]});
            var Q16;
            Q16=makeQuery(id+"F1.imprint","IMPRINT",FACE,{"disambiguationData":[TD([[makeQuery(id+"F1.imprint","IMPRINT",EDGE,{"derivedFrom":sQuery(id+"F1.wireOp",EDGE,"E179.MirrorC")}),1.0]])]});
            var Q17;
            Q17=makeQuery(id+"F1.imprint","IMPRINT",FACE,{"disambiguationData":[TD([[makeQuery(id+"F1.imprint","IMPRINT",EDGE,{"derivedFrom":sQuery(id+"F1.wireOp",EDGE,"E180.MirrorC")}),-1.0]])]});
            var Q18;
            Q18=makeQuery(id+"F1.imprint","IMPRINT",FACE,{"disambiguationData":[TD([[makeQuery(id+"F1.imprint","IMPRINT",EDGE,{"derivedFrom":sQuery(id+"F1.wireOp",EDGE,"E181.MirrorC")}),1.0]])]});
            var Q19;
            Q19=makeQuery(id+"F1.imprint","IMPRINT",FACE,{"disambiguationData":[TD([[makeQuery(id+"F1.imprint","IMPRINT",EDGE,{"derivedFrom":sQuery(id+"F1.wireOp",EDGE,"E182.MirrorC")}),-1.0]])]});
            extrude(context, id + "F2", {"entities" : qUnion([Q0, Q1, Q2, Q3, Q4, Q5, Q6, Q7, Q8, Q9, Q10, Q11, Q12, Q13, Q14, Q15, Q16, Q17, Q18, Q19]), "depth" : 4 * mm});
        }
        {
            var Q0;
            {var subQ0=sQuery(id+"F1.wireOp",EDGE,"E97");var subQ8=makeQuery(id+"F1.imprint","INTERSECT",VERTEX,{"derivedFrom":[subQ0,sQuery(id+"F1.wireOp",EDGE,"E138.MirrorCS")]});Q0=makeQuery(id+"F1.imprint","IMPRINT",FACE,{"disambiguationData":[TD([[makeQuery(id+"F1.imprint","IMPRINT",EDGE,{"disambiguationData":[TD([[subQ8,1.0]])],"derivedFrom":subQ0}),1.0]])]});}
            extrude(context, id + "F3", {"entities" : qUnion([Q0]), "operationType" : NewBodyOperationType.REMOVE, "depth" : 1 * mm});
        }
        {
            var Q0;
            Q0=makeQuery(id+"F1.imprint","IMPRINT",FACE,{"disambiguationData":[TD([[makeQuery(id+"F1.imprint","IMPRINT",EDGE,{"derivedFrom":sQuery(id+"F1.wireOp",EDGE,"E179.MirrorC")}),1.0]])]});
            var Q1;
            {var subQ0=sQuery(id+"F1.wireOp",EDGE,"E97");var subQ8=makeQuery(id+"F1.imprint","INTERSECT",VERTEX,{"derivedFrom":[subQ0,sQuery(id+"F1.wireOp",EDGE,"E138.MirrorCS")]});Q1=makeQuery(id+"F1.imprint","IMPRINT",FACE,{"disambiguationData":[TD([[makeQuery(id+"F1.imprint","IMPRINT",EDGE,{"disambiguationData":[TD([[subQ8,1.0]])],"derivedFrom":subQ0}),1.0]])]});}
            var Q2;
            Q2=makeQuery(id+"F1.imprint","IMPRINT",FACE,{"disambiguationData":[TD([[makeQuery(id+"F1.imprint","IMPRINT",EDGE,{"derivedFrom":sQuery(id+"F1.wireOp",EDGE,"E102.top")}),-1.0]])]});
            var Q3;
            Q3=makeQuery(id+"F1.imprint","IMPRINT",FACE,{"disambiguationData":[TD([[makeQuery(id+"F1.imprint","IMPRINT",EDGE,{"derivedFrom":sQuery(id+"F1.wireOp",EDGE,"E102.top")}),1.0]])]});
            var Q4;
            {var subQ0=sQuery(id+"F1.wireOp",EDGE,"E137.MirrorCS");Q4=makeQuery(id+"F1.imprint","IMPRINT",FACE,{"disambiguationData":[TD([[makeQuery(id+"F1.imprint","IMPRINT",EDGE,{"derivedFrom":subQ0}),-1.0]])]});}
            var Q5;
            Q5=makeQuery(id+"F1.imprint","IMPRINT",FACE,{"disambiguationData":[TD([[makeQuery(id+"F1.imprint","IMPRINT",EDGE,{"derivedFrom":sQuery(id+"F1.wireOp",EDGE,"E111")}),1.0]])]});
            var Q6;
            Q6=makeQuery(id+"F1.imprint","IMPRINT",FACE,{"disambiguationData":[TD([[makeQuery(id+"F1.imprint","IMPRINT",EDGE,{"derivedFrom":sQuery(id+"F1.wireOp",EDGE,"E111")}),-1.0]])]});
            var Q7;
            Q7=makeQuery(id+"F1.imprint","IMPRINT",FACE,{"disambiguationData":[TD([[makeQuery(id+"F1.imprint","IMPRINT",EDGE,{"derivedFrom":sQuery(id+"F1.wireOp",EDGE,"E107")}),1.0]])]});
            var Q8;
            {var subQ0=sQuery(id+"F1.wireOp",EDGE,"E139");Q8=makeQuery(id+"F1.imprint","IMPRINT",FACE,{"disambiguationData":[TD([[makeQuery(id+"F1.imprint","IMPRINT",EDGE,{"derivedFrom":subQ0}),1.0]])]});}
            var Q9;
            Q9=makeQuery(id+"F1.imprint","IMPRINT",FACE,{"disambiguationData":[TD([[makeQuery(id+"F1.imprint","IMPRINT",EDGE,{"derivedFrom":sQuery(id+"F1.wireOp",EDGE,"E98.bottom")}),-1.0]])]});
            var Q10;
            Q10=makeQuery(id+"F1.imprint","IMPRINT",FACE,{"disambiguationData":[TD([[makeQuery(id+"F1.imprint","IMPRINT",EDGE,{"derivedFrom":sQuery(id+"F1.wireOp",EDGE,"E107")}),-1.0]])]});
            var Q11;
            {var subQ0=sQuery(id+"F1.wireOp",EDGE,"E150");Q11=makeQuery(id+"F1.imprint","IMPRINT",FACE,{"disambiguationData":[TD([[makeQuery(id+"F1.imprint","IMPRINT",EDGE,{"derivedFrom":subQ0}),1.0]])]});}
            var Q12;
            Q12=makeQuery(id+"F1.imprint","IMPRINT",FACE,{"disambiguationData":[TD([[makeQuery(id+"F1.imprint","IMPRINT",EDGE,{"derivedFrom":sQuery(id+"F1.wireOp",EDGE,"E98.bottom")}),1.0]])]});
            var Q13;
            {var subQ0=sQuery(id+"F1.wireOp",EDGE,"E147");Q13=makeQuery(id+"F1.imprint","IMPRINT",FACE,{"disambiguationData":[TD([[makeQuery(id+"F1.imprint","IMPRINT",EDGE,{"derivedFrom":subQ0}),1.0]])]});}
            var Q14;
            Q14=makeQuery(id+"F1.imprint","IMPRINT",FACE,{"disambiguationData":[TD([[makeQuery(id+"F1.imprint","IMPRINT",EDGE,{"derivedFrom":sQuery(id+"F1.wireOp",EDGE,"E103")}),-1.0]])]});
            var Q15;
            Q15=makeQuery(id+"F1.imprint","IMPRINT",FACE,{"disambiguationData":[TD([[makeQuery(id+"F1.imprint","IMPRINT",EDGE,{"derivedFrom":sQuery(id+"F1.wireOp",EDGE,"E115")}),-1.0]])]});
            var Q16;
            {var subQ0=sQuery(id+"F1.wireOp",EDGE,"E144.MirrorCS");Q16=makeQuery(id+"F1.imprint","IMPRINT",FACE,{"disambiguationData":[TD([[makeQuery(id+"F1.imprint","IMPRINT",EDGE,{"derivedFrom":subQ0}),-1.0]])]});}
            var Q17;
            {var subQ0=sQuery(id+"F1.wireOp",EDGE,"E135");Q17=makeQuery(id+"F1.imprint","IMPRINT",FACE,{"disambiguationData":[TD([[makeQuery(id+"F1.imprint","IMPRINT",EDGE,{"derivedFrom":subQ0}),1.0]])]});}
            var Q18;
            Q18=makeQuery(id+"F1.imprint","IMPRINT",FACE,{"disambiguationData":[TD([[makeQuery(id+"F1.imprint","IMPRINT",EDGE,{"derivedFrom":sQuery(id+"F1.wireOp",EDGE,"E115")}),1.0]])]});
            var Q19;
            Q19=makeQuery(id+"F1.imprint","IMPRINT",FACE,{"disambiguationData":[TD([[makeQuery(id+"F1.imprint","IMPRINT",EDGE,{"derivedFrom":sQuery(id+"F1.wireOp",EDGE,"E103")}),1.0]])]});
            var Q20;
            {var subQ3=sQuery(id+"F1.wireOp",EDGE,"E165");Q20=makeQuery(id+"F1.imprint","IMPRINT",FACE,{"disambiguationData":[TD([[makeQuery(id+"F1.imprint","IMPRINT",EDGE,{"derivedFrom":subQ3}),1.0]])]});}
            var Q21;
            Q21=makeQuery(id+"F1.imprint","IMPRINT",FACE,{"disambiguationData":[TD([[makeQuery(id+"F1.imprint","IMPRINT",EDGE,{"derivedFrom":sQuery(id+"F1.wireOp",EDGE,"E180.MirrorC")}),-1.0]])]});
            var Q22;
            Q22=makeQuery(id+"F1.imprint","IMPRINT",FACE,{"disambiguationData":[TD([[makeQuery(id+"F1.imprint","IMPRINT",EDGE,{"derivedFrom":sQuery(id+"F1.wireOp",EDGE,"E183.MirrorC")}),1.0]])]});
            var Q23;
            Q23=makeQuery(id+"F1.imprint","IMPRINT",FACE,{"disambiguationData":[TD([[makeQuery(id+"F1.imprint","IMPRINT",EDGE,{"derivedFrom":sQuery(id+"F1.wireOp",EDGE,"E178")}),-1.0]])]});
            var Q24;
            Q24=makeQuery(id+"F1.imprint","IMPRINT",FACE,{"disambiguationData":[TD([[makeQuery(id+"F1.imprint","IMPRINT",EDGE,{"derivedFrom":sQuery(id+"F1.wireOp",EDGE,"E181.MirrorC")}),1.0]])]});
            var Q25;
            Q25=makeQuery(id+"F1.imprint","IMPRINT",FACE,{"disambiguationData":[TD([[makeQuery(id+"F1.imprint","IMPRINT",EDGE,{"derivedFrom":sQuery(id+"F1.wireOp",EDGE,"E182.MirrorC")}),-1.0]])]});
            var Q26;
            {var subQ3=sQuery(id+"F1.wireOp",EDGE,"E175.MirrorCS");Q26=makeQuery(id+"F1.imprint","IMPRINT",FACE,{"disambiguationData":[TD([[makeQuery(id+"F1.imprint","IMPRINT",EDGE,{"derivedFrom":subQ3}),-1.0]])]});}
            var Q27;
            {var subQ3=sQuery(id+"F1.wireOp",EDGE,"E173.MirrorCS");Q27=makeQuery(id+"F1.imprint","IMPRINT",FACE,{"disambiguationData":[TD([[makeQuery(id+"F1.imprint","IMPRINT",EDGE,{"derivedFrom":subQ3}),-1.0]])]});}
            var Q28;
            {var subQ3=sQuery(id+"F1.wireOp",EDGE,"E167.MirrorCS");Q28=makeQuery(id+"F1.imprint","IMPRINT",FACE,{"disambiguationData":[TD([[makeQuery(id+"F1.imprint","IMPRINT",EDGE,{"derivedFrom":subQ3}),-1.0]])]});}
            var Q29;
            {var subQ3=sQuery(id+"F1.wireOp",EDGE,"E171.MirrorCS");Q29=makeQuery(id+"F1.imprint","IMPRINT",FACE,{"disambiguationData":[TD([[makeQuery(id+"F1.imprint","IMPRINT",EDGE,{"derivedFrom":subQ3}),-1.0]])]});}
            var Q30;
            {var subQ3=sQuery(id+"F1.wireOp",EDGE,"E169.MirrorCS");Q30=makeQuery(id+"F1.imprint","IMPRINT",FACE,{"disambiguationData":[TD([[makeQuery(id+"F1.imprint","IMPRINT",EDGE,{"derivedFrom":subQ3}),-1.0]])]});}
            var Q31;
            Q31=makeQuery(id+"F1.imprint","IMPRINT",FACE,{"disambiguationData":[TD([[makeQuery(id+"F1.imprint","IMPRINT",EDGE,{"derivedFrom":sQuery(id+"F1.wireOp",EDGE,"E177")}),-1.0]])]});
            extrude(context, id + "F4", {"entities" : qUnion([Q0, Q1, Q2, Q3, Q4, Q5, Q6, Q7, Q8, Q9, Q10, Q11, Q12, Q13, Q14, Q15, Q16, Q17, Q18, Q19, Q20, Q21, Q22, Q23, Q24, Q25, Q26, Q27, Q28, Q29, Q30, Q31]), "depth" : 4 * mm});
        }
        {
            var Q0;
            {var subQ0=sQuery(id+"F1.wireOp",EDGE,"E97");var subQ8=makeQuery(id+"F1.imprint","INTERSECT",VERTEX,{"derivedFrom":[subQ0,sQuery(id+"F1.wireOp",EDGE,"E138.MirrorCS")]});Q0=makeQuery(id+"F1.imprint","IMPRINT",FACE,{"disambiguationData":[TD([[makeQuery(id+"F1.imprint","IMPRINT",EDGE,{"disambiguationData":[TD([[subQ8,1.0]])],"derivedFrom":subQ0}),1.0]])]});}
            extrude(context, id + "F5", {"entities" : qUnion([Q0]), "operationType" : NewBodyOperationType.REMOVE, "depth" : 1 * mm});
        }
        {
            var Q0;
            Q0=makeQuery(id+"F2.opExtrude","CAP_FACE",FACE,{"disambiguationData":[OSD([sQuery(id+"F1.wireOp",EDGE,"E97"),sQuery(id+"F1.wireOp",EDGE,"E98.bottom"),sQuery(id+"F1.wireOp",EDGE,"E98.left"),sQuery(id+"F1.wireOp",EDGE,"E98.right"),sQuery(id+"F1.wireOp",EDGE,"E102.top"),sQuery(id+"F1.wireOp",EDGE,"E102.left"),sQuery(id+"F1.wireOp",EDGE,"E102.right"),sQuery(id+"F1.wireOp",EDGE,"E103"),sQuery(id+"F1.wireOp",EDGE,"E104"),sQuery(id+"F1.wireOp",EDGE,"E105"),sQuery(id+"F1.wireOp",EDGE,"E106"),sQuery(id+"F1.wireOp",EDGE,"E107"),sQuery(id+"F1.wireOp",EDGE,"E108"),sQuery(id+"F1.wireOp",EDGE,"E109"),sQuery(id+"F1.wireOp",EDGE,"E110"),sQuery(id+"F1.wireOp",EDGE,"E111"),sQuery(id+"F1.wireOp",EDGE,"E112"),sQuery(id+"F1.wireOp",EDGE,"E113"),sQuery(id+"F1.wireOp",EDGE,"E114"),sQuery(id+"F1.wireOp",EDGE,"E115"),sQuery(id+"F1.wireOp",EDGE,"E116"),sQuery(id+"F1.wireOp",EDGE,"E117"),sQuery(id+"F1.wireOp",EDGE,"E118"),sQuery(id+"F1.wireOp",EDGE,"E127.0"),sQuery(id+"F1.wireOp",EDGE,"E127.1"),sQuery(id+"F1.wireOp",EDGE,"E127.2"),sQuery(id+"F1.wireOp",EDGE,"E127.3"),sQuery(id+"F1.wireOp",EDGE,"E127.4"),sQuery(id+"F1.wireOp",EDGE,"E127.5"),sQuery(id+"F1.wireOp",EDGE,"E135"),sQuery(id+"F1.wireOp",EDGE,"E136.MirrorCS"),sQuery(id+"F1.wireOp",EDGE,"E137.MirrorCS"),sQuery(id+"F1.wireOp",EDGE,"E138.MirrorCS"),sQuery(id+"F1.wireOp",EDGE,"E139"),sQuery(id+"F1.wireOp",EDGE,"E140.MirrorCS"),sQuery(id+"F1.wireOp",EDGE,"E144.MirrorCS"),sQuery(id+"F1.wireOp",EDGE,"E145.MirrorCS"),sQuery(id+"F1.wireOp",EDGE,"E147"),sQuery(id+"F1.wireOp",EDGE,"E148.MirrorCS"),sQuery(id+"F1.wireOp",EDGE,"E150"),sQuery(id+"F1.wireOp",EDGE,"E151.MirrorCS"),sQuery(id+"F1.wireOp",EDGE,"E164.0"),sQuery(id+"F1.wireOp",EDGE,"E164.1"),sQuery(id+"F1.wireOp",EDGE,"E164.2"),sQuery(id+"F1.wireOp",EDGE,"E164.3"),sQuery(id+"F1.wireOp",EDGE,"E164.4"),sQuery(id+"F1.wireOp",EDGE,"E164.5"),sQuery(id+"F1.wireOp",EDGE,"E165"),sQuery(id+"F1.wireOp",EDGE,"E166.MirrorCS"),sQuery(id+"F1.wireOp",EDGE,"E167.MirrorCS"),sQuery(id+"F1.wireOp",EDGE,"E168.MirrorCS"),sQuery(id+"F1.wireOp",EDGE,"E169.MirrorCS"),sQuery(id+"F1.wireOp",EDGE,"E170.MirrorCS"),sQuery(id+"F1.wireOp",EDGE,"E171.MirrorCS"),sQuery(id+"F1.wireOp",EDGE,"E172.MirrorCS"),sQuery(id+"F1.wireOp",EDGE,"E173.MirrorCS"),sQuery(id+"F1.wireOp",EDGE,"E174.MirrorCS"),sQuery(id+"F1.wireOp",EDGE,"E175.MirrorCS"),sQuery(id+"F1.wireOp",EDGE,"E176.MirrorCS"),sQuery(id+"F1.wireOp",EDGE,"E177"),sQuery(id+"F1.wireOp",EDGE,"E178"),sQuery(id+"F1.wireOp",EDGE,"E179.MirrorC"),sQuery(id+"F1.wireOp",EDGE,"E180.MirrorC"),sQuery(id+"F1.wireOp",EDGE,"E181.MirrorC"),sQuery(id+"F1.wireOp",EDGE,"E182.MirrorC"),sQuery(id+"F1.wireOp",EDGE,"E183.MirrorC"),sQuery(id+"F1.wireOp",EDGE,"E188"),sQuery(id+"F1.wireOp",EDGE,"E190")])],"isStart":false});
            var sketch = newSketch(context, id + "F6", { "sketchPlane" : qUnion([Q0])});
            skCircle(sketch, "E191", {"center": v(0, 0) * mm, "radius": 37.5 * mm});
            skCircle(sketch, "E192", {"center": v(0, 0) * mm, "radius": 35 * mm});
            skSolve(sketch);
        }
        {
            var Q0;
            Q0 = qSketchRegion(id + "F6", true);
            extrude(context, id + "F7", {"entities" : qUnion([Q0]), "operationType" : NewBodyOperationType.REMOVE, "oppositeDirection" : true, "depth" : 1 * mm});
        }
        {
            var Q0;
            Q0=makeQuery(id+"F6.imprint","IMPRINT",FACE,{"disambiguationData":[TD([[makeQuery(id+"F6.imprint","IMPRINT",EDGE,{"derivedFrom":sQuery(id+"F6.wireOp",EDGE,"E192")}),-1.0]])]});
            extrude(context, id + "F8", {"entities" : qUnion([Q0]), "depth" : 32 * mm});
        }
        {
            var Q0;
            Q0=makeQuery(id+"F6.imprint","IMPRINT",FACE,{"disambiguationData":[TD([[makeQuery(id+"F6.imprint","IMPRINT",EDGE,{"derivedFrom":sQuery(id+"F6.wireOp",EDGE,"E192")}),-1.0]])]});
            extrude(context, id + "F9", {"entities" : qUnion([Q0]), "depth" : 13 * mm});
        }
        {
            var Q0;
            Q0=qCreatedBy(makeId("Top.planeOp"),FACE);
            cPlane(context, id + "F10", {"entities" : qUnion([Q0]), "cplaneType" : CPlaneType.OFFSET, "offset" : 79 * mm, "oppositeDirection" : true, "width" : 150 * mm, "height" : 150 * mm});
        }
        {
            var Q0;
            Q0=qCreatedBy(id+"F10.planeOp",FACE);
            var sketch = newSketch(context, id + "F11", { "sketchPlane" : qUnion([Q0])});
            skLineSegment(sketch, "E193.bottom", {"start": v(30, 15) * mm, "end": v(-30, 15) * mm});
            skLineSegment(sketch, "E193.top", {"start": v(30, -15) * mm, "end": v(-30, -15) * mm});
            skLineSegment(sketch, "E193.left", {"start": v(30, 15) * mm, "end": v(30, -15) * mm});
            skLineSegment(sketch, "E193.right", {"start": v(-30, 15) * mm, "end": v(-30, -15) * mm});
            skPoint(sketch, "E193.middle", {"position": v(0, 0) * mm});
            skSolve(sketch);
        }
        {
            var Q0;
            Q0 = qSketchRegion(id + "F11", true);
            extrude(context, id + "F12", {"entities" : qUnion([Q0]), "depth" : 2 * mm});
        }
    });
